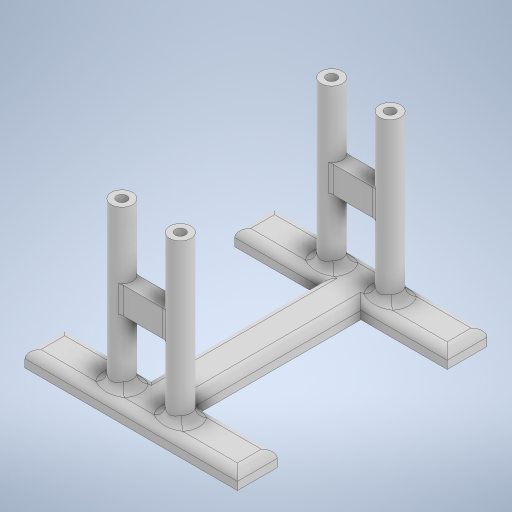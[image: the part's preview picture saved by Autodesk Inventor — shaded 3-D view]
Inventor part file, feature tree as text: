
AUTODESK INVENTOR PART (.ipt)
format: ipt  version: 2023.2 (Build 272271030, 271C)  size: 439,808 bytes
history: native  units: mm
features: extrude x4, sketch x4, fillet x3, projected_geometry x2, plane x1, mirror x1
ambient origin geometry x8: Origin, YZ Plane, XZ Plane, XY Plane, X Axis, Y Axis, Z Axis, Center Point
bodies: Solid1 (feature_tree)
feature tree (15):
  extrude  "Extrusion1"  Depth=6.0mm
  fillet  "Fillet1"  Radius=6.0mm
  extrude  "Extrusion2"  Depth=3.0mm
  fillet  "Fillet2"  Radius=22.0mm
  extrude  "Extrusion3"  Depth=3.0mm
  plane  "Work Plane1"
  extrude  "Extrusion4"  Depth=3.0mm
  fillet  "Fillet3"  Radius=39.5mm
  mirror  "Mirror1"
  sketch  "Sketch1"  dims[d0=80.0mm d1=15.0mm d2=6.0mm d3=0.0mm]
  sketch  "Sketch2"  dims[d4=3.0mm d5=8.0mm d6=22.0mm]
  projected_geometry  "Projected Loop1"
  sketch  "Sketch3"  dims[d7=60.0mm d8=0.0mm d9=3.0mm]
  projected_geometry  "Projected Loop2"
  sketch  "Sketch4"  dims[d10=3.75mm d11=3.75mm d12=39.5mm d13=79.0mm d14=7.5mm d15=7.5mm d16=6.0mm d17=0.0mm d18=11.0mm d19=6.0mm d20=10.0mm d21=25.0mm d23=1.0mm d24=22.0mm d25=0.0mm d26=3.0mm]
